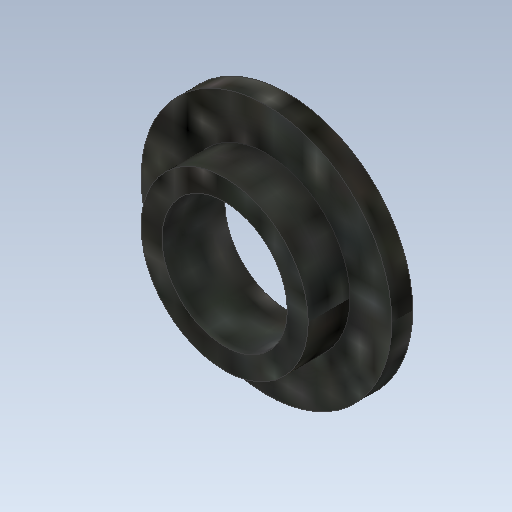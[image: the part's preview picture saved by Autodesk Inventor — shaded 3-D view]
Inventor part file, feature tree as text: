
AUTODESK INVENTOR PART (.ipt)
format: ipt  version: 2020.2 (Build 242310000, 310)  size: 160,768 bytes
history: native  units: mm
features: extrude x2, other x1, sketch x1
ambient origin geometry x8: Origin, YZ Plane, XZ Plane, XY Plane, X Axis, Y Axis, Z Axis, Center Point
bodies: Body1 (feature_tree)
feature tree (4):
  other  "ソリッド1"
  sketch  "スケッチ1"
  extrude  "押し出し1"  Depth=6.0mm
  extrude  "押し出し2"  Depth=8.0mm
